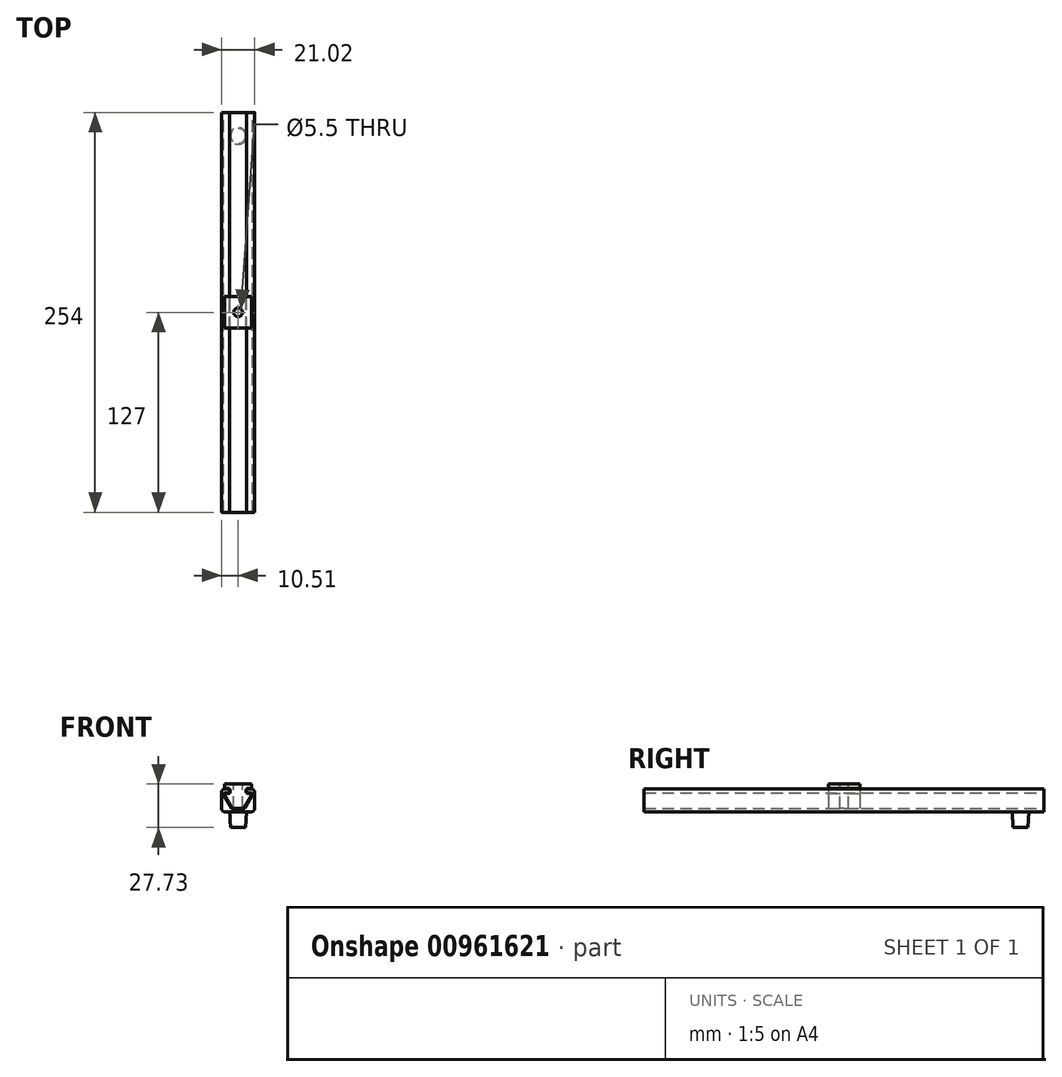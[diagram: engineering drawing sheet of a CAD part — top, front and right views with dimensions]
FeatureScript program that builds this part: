
annotation { "Feature Type Name" : "Feature", "Feature Type Description" : "" }
export const myFeature = defineFeature(function(context is Context, id is Id, definition is map)
    precondition{}
    {
        {
            var Q0;
            Q0=qCreatedBy(makeId("Front.planeOp"),FACE);
            var sketch = newSketch(context, id + "F0", { "sketchPlane" : qUnion([Q0])});
            skLineSegment(sketch, "E0.bottom", {"start": v(8.5, 7.23) * mm, "end": v(6, 7.23) * mm});
            skLineSegment(sketch, "E0.top", {"start": v(8.5, -7.23) * mm, "end": v(-8.5, -7.23) * mm});
            skLineSegment(sketch, "E0.left", {"start": v(10.5, 5.23) * mm, "end": v(10.5, -5.23) * mm});
            skLineSegment(sketch, "E0.right", {"start": v(-10.5, 5.23) * mm, "end": v(-10.5, -5.23) * mm});
            skPoint(sketch, "E0.middle", {"position": v(0, 0) * mm});
            skLineSegment(sketch, "E1", {"start": v(5.5, 6.73) * mm, "end": v(5.5, 5.23) * mm});
            skLineSegment(sketch, "E2", {"start": v(6, 4.73) * mm, "end": v(8.14, 4.73) * mm});
            skLineSegment(sketch, "E3", {"start": v(3.43, -5.22) * mm, "end": v(0, -5.22) * mm});
            skLineSegment(sketch, "E4.MirrorCS", {"start": v(-5.5, 6.73) * mm, "end": v(-5.5, 5.23) * mm});
            skLineSegment(sketch, "E5.MirrorCS", {"start": v(-6, 4.73) * mm, "end": v(-8.14, 4.73) * mm});
            skLineSegment(sketch, "E6.MirrorCS", {"start": v(-3.43, -5.22) * mm, "end": v(0, -5.22) * mm});
            skLineSegment(sketch, "E7.trimOffspring", {"start": v(-6, 7.23) * mm, "end": v(-8.5, 7.23) * mm});
            skLineSegment(sketch, "E8", {"start": v(9, 3.22) * mm, "end": v(4.3, -4.73) * mm});
            skPoint(sketch, "E9.orphan", {"position": v(8, -5.22) * mm});
            skLineSegment(sketch, "E10.MirrorCS", {"start": v(-9, 3.22) * mm, "end": v(-4.3, -4.73) * mm});
            skPoint(sketch, "E11.MirrorCS.end.orphan", {"position": v(-8, -5.22) * mm});
            skPoint(sketch, "E11.MirrorCS.start.orphan", {"position": v(-9.9, 4.73) * mm});
            skPoint(sketch, "E12.visualSharp", {"position": v(-10.5, 7.23) * mm});
            skArc(sketch, "E12.filletArc", {"start": v(-8.5, 7.23) * mm, "mid": v(-9.92, 6.64) * mm, "end": v(-10.5, 5.23) * mm});
            skPoint(sketch, "E13.visualSharp", {"position": v(-10.5, -7.23) * mm});
            skArc(sketch, "E13.filletArc", {"start": v(-10.5, -5.23) * mm, "mid": v(-9.92, -6.64) * mm, "end": v(-8.5, -7.23) * mm});
            skPoint(sketch, "E14.visualSharp", {"position": v(10.5, 7.23) * mm});
            skArc(sketch, "E14.filletArc", {"start": v(10.5, 5.23) * mm, "mid": v(9.92, 6.64) * mm, "end": v(8.5, 7.23) * mm});
            skPoint(sketch, "E15.visualSharp", {"position": v(10.5, -7.23) * mm});
            skArc(sketch, "E15.filletArc", {"start": v(8.5, -7.23) * mm, "mid": v(9.92, -6.64) * mm, "end": v(10.5, -5.23) * mm});
            skPoint(sketch, "E16.visualSharp", {"position": v(9.9, 4.73) * mm});
            skArc(sketch, "E16.filletArc", {"start": v(9, 3.22) * mm, "mid": v(9, 4.22) * mm, "end": v(8.14, 4.73) * mm});
            skArc(sketch, "E17.filletArc", {"start": v(-8.14, 4.73) * mm, "mid": v(-9, 4.22) * mm, "end": v(-9, 3.22) * mm});
            skPoint(sketch, "E18.visualSharp", {"position": v(4, -5.22) * mm});
            skArc(sketch, "E18.filletArc", {"start": v(3.43, -5.22) * mm, "mid": v(3.93, -5.09) * mm, "end": v(4.3, -4.73) * mm});
            skPoint(sketch, "E19.visualSharp", {"position": v(-4, -5.22) * mm});
            skArc(sketch, "E19.filletArc", {"start": v(-4.3, -4.73) * mm, "mid": v(-3.93, -5.09) * mm, "end": v(-3.43, -5.22) * mm});
            skPoint(sketch, "E20.visualSharp", {"position": v(5.5, 4.73) * mm});
            skArc(sketch, "E20.filletArc", {"start": v(5.5, 5.23) * mm, "mid": v(5.64, 4.88) * mm, "end": v(6, 4.73) * mm});
            skPoint(sketch, "E21.visualSharp", {"position": v(5.5, 7.23) * mm});
            skArc(sketch, "E21.filletArc", {"start": v(6, 7.23) * mm, "mid": v(5.64, 7.08) * mm, "end": v(5.5, 6.73) * mm});
            skPoint(sketch, "E22.visualSharp", {"position": v(-5.5, 7.23) * mm});
            skArc(sketch, "E22.filletArc", {"start": v(-5.5, 6.73) * mm, "mid": v(-5.64, 7.08) * mm, "end": v(-6, 7.23) * mm});
            skPoint(sketch, "E23.visualSharp", {"position": v(-5.5, 4.73) * mm});
            skArc(sketch, "E23.filletArc", {"start": v(-6, 4.73) * mm, "mid": v(-5.64, 4.88) * mm, "end": v(-5.5, 5.23) * mm});
            skSolve(sketch);
        }
        {
            var Q0;
            Q0 = qSketchRegion(id + "F0", true);
            extrude(context, id + "F1", {"entities" : qUnion([Q0]), "endBound" : BoundingType.SYMMETRIC, "depth" : 254 * mm, "offsetDistance" : 25 * mm});
        }
        {
            var Q0;
            Q0=qCreatedBy(makeId("Front.planeOp"),FACE);
            var sketch = newSketch(context, id + "F2", { "sketchPlane" : qUnion([Q0])});
            skLineSegment(sketch, "E24.0.0", {"start": v(-8.14, 4.73) * mm, "end": v(-6, 4.73) * mm, "construction": true});
            skArc(sketch, "E24.0.1", {"start": v(-6, 4.73) * mm, "mid": v(-5.64, 4.88) * mm, "end": v(-5.5, 5.23) * mm, "construction": true});
            skLineSegment(sketch, "E24.0.2", {"start": v(-5.5, 5.23) * mm, "end": v(-5.5, 6.73) * mm, "construction": true});
            skArc(sketch, "E24.0.3", {"start": v(-5.5, 6.73) * mm, "mid": v(-5.64, 7.08) * mm, "end": v(-6, 7.23) * mm, "construction": true});
            skLineSegment(sketch, "E24.0.4", {"start": v(-6, 7.23) * mm, "end": v(-8.5, 7.23) * mm, "construction": true});
            skArc(sketch, "E24.0.5", {"start": v(-8.5, 7.23) * mm, "mid": v(-9.92, 6.64) * mm, "end": v(-10.5, 5.23) * mm, "construction": true});
            skLineSegment(sketch, "E24.0.6", {"start": v(-10.5, 5.23) * mm, "end": v(-10.5, -5.23) * mm, "construction": true});
            skArc(sketch, "E24.0.7", {"start": v(-10.5, -5.23) * mm, "mid": v(-9.92, -6.64) * mm, "end": v(-8.5, -7.23) * mm, "construction": true});
            skLineSegment(sketch, "E24.0.8", {"start": v(-8.5, -7.23) * mm, "end": v(8.5, -7.23) * mm, "construction": true});
            skArc(sketch, "E24.0.9", {"start": v(8.5, -7.23) * mm, "mid": v(9.92, -6.64) * mm, "end": v(10.5, -5.23) * mm, "construction": true});
            skLineSegment(sketch, "E24.0.10", {"start": v(10.5, -5.23) * mm, "end": v(10.5, 5.23) * mm, "construction": true});
            skArc(sketch, "E24.0.11", {"start": v(10.5, 5.23) * mm, "mid": v(9.92, 6.64) * mm, "end": v(8.5, 7.23) * mm, "construction": true});
            skLineSegment(sketch, "E24.0.12", {"start": v(8.5, 7.23) * mm, "end": v(6, 7.23) * mm, "construction": true});
            skArc(sketch, "E24.0.13", {"start": v(6, 7.23) * mm, "mid": v(5.64, 7.08) * mm, "end": v(5.5, 6.73) * mm, "construction": true});
            skLineSegment(sketch, "E24.0.14", {"start": v(5.5, 6.73) * mm, "end": v(5.5, 5.23) * mm, "construction": true});
            skArc(sketch, "E24.0.15", {"start": v(5.5, 5.23) * mm, "mid": v(5.64, 4.88) * mm, "end": v(6, 4.73) * mm, "construction": true});
            skLineSegment(sketch, "E24.0.16", {"start": v(6, 4.73) * mm, "end": v(8.14, 4.73) * mm, "construction": true});
            skArc(sketch, "E24.0.17", {"start": v(8.14, 4.73) * mm, "mid": v(9, 4.22) * mm, "end": v(9, 3.22) * mm, "construction": true});
            skLineSegment(sketch, "E24.0.18", {"start": v(9, 3.22) * mm, "end": v(4.3, -4.73) * mm, "construction": true});
            skArc(sketch, "E24.0.19", {"start": v(4.3, -4.73) * mm, "mid": v(3.93, -5.09) * mm, "end": v(3.43, -5.22) * mm, "construction": true});
            skLineSegment(sketch, "E24.0.20", {"start": v(3.43, -5.22) * mm, "end": v(-3.43, -5.22) * mm, "construction": true});
            skArc(sketch, "E24.0.21", {"start": v(-3.43, -5.22) * mm, "mid": v(-3.93, -5.09) * mm, "end": v(-4.3, -4.73) * mm, "construction": true});
            skLineSegment(sketch, "E24.0.22", {"start": v(-4.3, -4.73) * mm, "end": v(-9, 3.22) * mm, "construction": true});
            skArc(sketch, "E24.0.23", {"start": v(-9, 3.22) * mm, "mid": v(-9, 4.22) * mm, "end": v(-8.14, 4.73) * mm, "construction": true});
            skLineSegment(sketch, "E25.0", {"start": v(8.5, 7.53) * mm, "end": v(6, 7.53) * mm});
            skArc(sketch, "E26.0", {"start": v(6, 7.53) * mm, "mid": v(5.43, 7.3) * mm, "end": v(5.2, 6.73) * mm});
            skLineSegment(sketch, "E27.0", {"start": v(5.2, 6.73) * mm, "end": v(5.2, 5.23) * mm});
            skArc(sketch, "E28.0", {"start": v(5.2, 5.23) * mm, "mid": v(5.43, 4.66) * mm, "end": v(6, 4.43) * mm});
            skLineSegment(sketch, "E29.0", {"start": v(6, 4.43) * mm, "end": v(8.14, 4.43) * mm});
            skLineSegment(sketch, "E30.0", {"start": v(8.74, 3.37) * mm, "end": v(4.03, -4.57) * mm});
            skArc(sketch, "E31.0", {"start": v(4.03, -4.57) * mm, "mid": v(3.78, -4.82) * mm, "end": v(3.43, -4.92) * mm});
            skLineSegment(sketch, "E32.0", {"start": v(3.43, -4.92) * mm, "end": v(-3.43, -4.92) * mm});
            skLineSegment(sketch, "E33.0", {"start": v(-4.03, -4.57) * mm, "end": v(-8.74, 3.37) * mm});
            skArc(sketch, "E33.1", {"start": v(-3.43, -4.92) * mm, "mid": v(-3.78, -4.82) * mm, "end": v(-4.03, -4.57) * mm});
            skArc(sketch, "E34.0", {"start": v(-8.74, 3.37) * mm, "mid": v(-8.74, 4.08) * mm, "end": v(-8.14, 4.43) * mm});
            skLineSegment(sketch, "E35.0", {"start": v(-5.2, 5.23) * mm, "end": v(-5.2, 6.73) * mm});
            skArc(sketch, "E35.1", {"start": v(-6, 4.43) * mm, "mid": v(-5.43, 4.66) * mm, "end": v(-5.2, 5.23) * mm});
            skLineSegment(sketch, "E35.2", {"start": v(-8.14, 4.43) * mm, "end": v(-6, 4.43) * mm});
            skLineSegment(sketch, "E36.0", {"start": v(-6, 7.53) * mm, "end": v(-8.5, 7.53) * mm});
            skArc(sketch, "E36.1", {"start": v(-5.2, 6.73) * mm, "mid": v(-5.43, 7.3) * mm, "end": v(-6, 7.53) * mm});
            skArc(sketch, "E37.0", {"start": v(8.14, 4.43) * mm, "mid": v(8.74, 4.08) * mm, "end": v(8.74, 3.37) * mm});
            skLineSegment(sketch, "E38", {"start": v(-8.5, 7.53) * mm, "end": v(-8.5, 10.5) * mm});
            skLineSegment(sketch, "E39", {"start": v(-8.5, 10.5) * mm, "end": v(8.5, 10.5) * mm});
            skLineSegment(sketch, "E40", {"start": v(8.5, 10.5) * mm, "end": v(8.5, 7.53) * mm});
            skSolve(sketch);
        }
        {
            var Q0;
            Q0 = qSketchRegion(id + "F2", true);
            extrude(context, id + "F3", {"entities" : qUnion([Q0]), "endBound" : BoundingType.SYMMETRIC, "depth" : 20 * mm, "offsetDistance" : 25 * mm});
        }
        {
            var Q0;
            Q0=makeQuery(id+"F3.opExtrude","SWEPT_FACE",FACE,{"disambiguationData":[OSD([sQuery(id+"F2.wireOp",EDGE,"E39")])]});
            var sketch = newSketch(context, id + "F4", { "sketchPlane" : qUnion([Q0])});
            skPoint(sketch, "E41", {"position": v(0, 0) * mm});
            skSolve(sketch);
        }
        {
            var Q0;
            Q0=sQuery(id+"F4.wireOp",VERTEX,"E41");
            var Q1;
            Q1=makeQuery(id+"F3.opExtrude","SWEPT_BODY",BODY,{"disambiguationData":[OSD([sQuery(id+"F2.wireOp",EDGE,"E25.0"),sQuery(id+"F2.wireOp",EDGE,"E26.0"),sQuery(id+"F2.wireOp",EDGE,"E27.0"),sQuery(id+"F2.wireOp",EDGE,"E28.0"),sQuery(id+"F2.wireOp",EDGE,"E29.0"),sQuery(id+"F2.wireOp",EDGE,"E30.0"),sQuery(id+"F2.wireOp",EDGE,"E31.0"),sQuery(id+"F2.wireOp",EDGE,"E32.0"),sQuery(id+"F2.wireOp",EDGE,"E33.0"),sQuery(id+"F2.wireOp",EDGE,"E33.1"),sQuery(id+"F2.wireOp",EDGE,"E34.0"),sQuery(id+"F2.wireOp",EDGE,"E35.0"),sQuery(id+"F2.wireOp",EDGE,"E35.1"),sQuery(id+"F2.wireOp",EDGE,"E35.2"),sQuery(id+"F2.wireOp",EDGE,"E36.0"),sQuery(id+"F2.wireOp",EDGE,"E36.1"),sQuery(id+"F2.wireOp",EDGE,"E37.0"),sQuery(id+"F2.wireOp",EDGE,"E38"),sQuery(id+"F2.wireOp",EDGE,"E39"),sQuery(id+"F2.wireOp",EDGE,"E40")])]});
            hole(context, id + "F5", {"style" : HoleStyle.SIMPLE, "endStyle" : HoleEndStyle.BLIND, "standardTappedOrClearance" : lookupTablePath({ "fit" : "Normal", "standard" : "ISO", "size" : "M5", "type" : "Clearance" }), "standardBlindInLast" : lookupTablePath({ "fit" : "Normal", "standard" : "ISO", "engagement" : "75%", "pitch" : "0.8 mm", "size" : "M5", "type" : "Clearance & tapped" }), "holeDiameter" : 5.5 * mm, "majorDiameter" : 5 * mm, "holeDepth" : 90 * mm, "isTappedThrough" : true, "tappedDepth" : 12 * mm, "tapClearance" : 3, "locations" : qUnion([Q0]), "scope" : qUnion([Q1])});
        }
        {
            var Q0;
            Q0=makeQuery(id+"F1.opExtrude","SWEPT_FACE",FACE,{"disambiguationData":[OSD([sQuery(id+"F0.wireOp",EDGE,"E0.top")])]});
            var sketch = newSketch(context, id + "F6", { "sketchPlane" : qUnion([Q0])});
            skCircle(sketch, "E42", {"center": v(0, -112.07) * mm, "radius": 5.33 * mm});
            skSolve(sketch);
        }
        {
            var Q0;
            Q0=makeQuery(id+"F6.imprint","IMPRINT",FACE,{"disambiguationData":[TD([[makeQuery(id+"F6.imprint","IMPRINT",EDGE,{"derivedFrom":sQuery(id+"F6.wireOp",EDGE,"E42")}),1.0]])]});
            extrude(context, id + "F7", {"entities" : qUnion([Q0]), "operationType" : NewBodyOperationType.ADD, "depth" : 10 * mm, "offsetDistance" : 25 * mm, "hasDraft" : true, "draftAngle" : 3 * degree, "draftPullDirection" : true});
        }
    });
